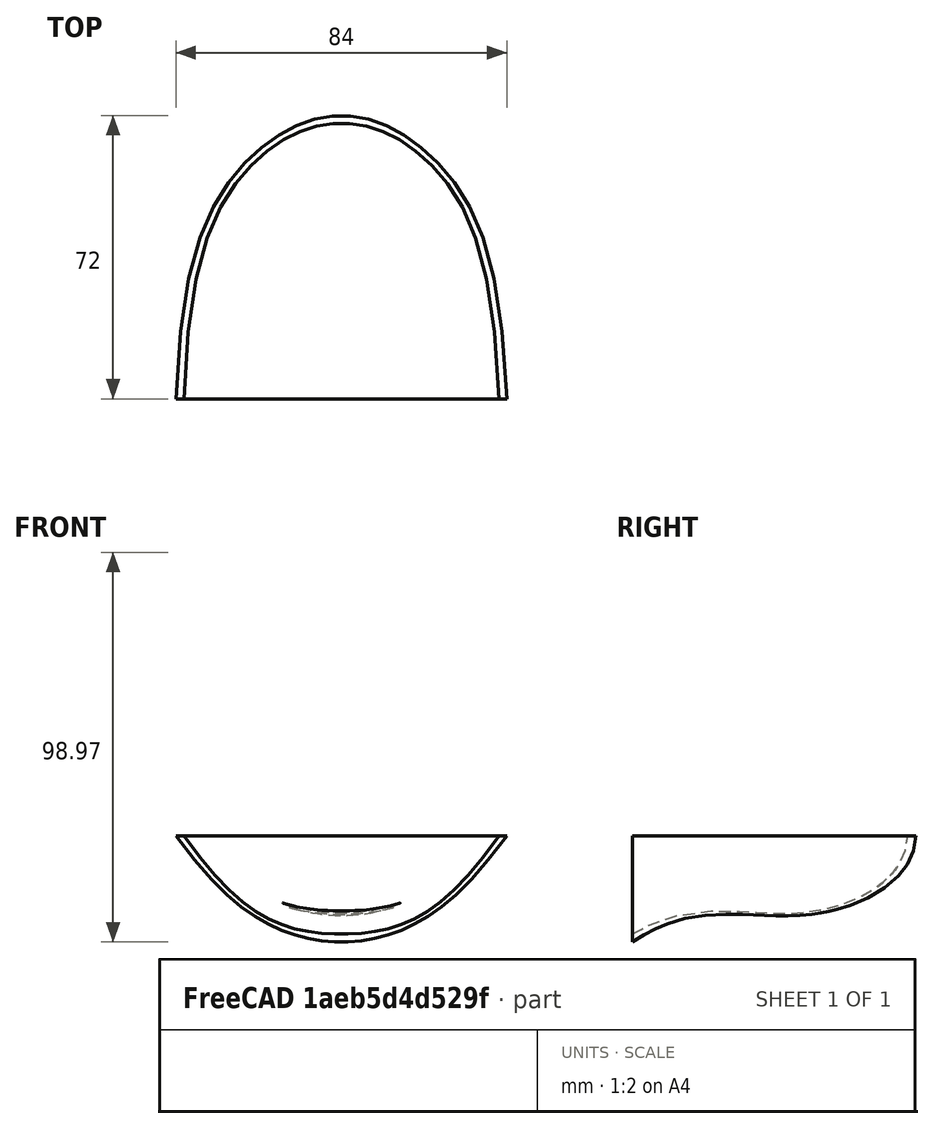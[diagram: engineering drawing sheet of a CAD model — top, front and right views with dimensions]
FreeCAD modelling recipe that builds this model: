
FCSTD DOCUMENT  (FreeCAD 0.21R33771 (Git))
Label: curved_surface_test
License: All rights reserved
LicenseURL: http://en.wikipedia.org/wiki/All_rights_reserved
objects: Sketcher::SketchObject×7, Surface::Filling×2, Part::RuledSurface×2, Part::Compound×1, Part::Feature×1, PartDesign::Body×1
note: 14 computed .brp shape members not serialized (recipe doc carries the construction recipe); baked Part::Feature solids carry a one-line shape summary decoded from their .brp

FEATURE [Sketcher::SketchObject] Sketch
  FullyConstrained = false
  MapMode = 5
  Support = -> [XY_Plane]
  sketch-geometry (13):
    g0-g6: Circle x7 (B-spline internal-alignment scaffolding for g7; pole/knot coordinates omitted)
    g7: BSplineCurve PolesCount=7 KnotsCount=5 Degree=3 IsPeriodic=0
    g8-g12: GeomPoint x5 (B-spline internal-alignment scaffolding for g7; pole/knot coordinates omitted)
  constraints (16):
    c: Weight(g0) = 1
    c: Equal(g0,g1)
    c: Equal(g0,g2)
    c: Equal(g0,g3)
    c: PointOnObject(g3,g-2)
    c: Equal(g0,g4)
    c: Equal(g0,g5)
    c: Equal(g0,g6)
    c: InternalAlignment(g0-g6 -> g7) x7
    c: InternalAlignment(g8-g12 -> g7) x5
    c: Symmetric(g7,g7,g-2)
    c: Symmetric(g1,g5,g-2)
    c: Symmetric(g9,g11,g-2)
    c: DistanceX(g0,g7) = 80
    c: DistanceY(g7,g-1) = 30
    c: DistanceY(g-1,g10) = 40
FEATURE [Sketcher::SketchObject] Sketch001
  FullyConstrained = false
  MapMode = 5
  Placement = pos=(0,0,0) rot=(0.57735,0.57735,0.57735;2.0944rad)
  Support = -> [YZ_Plane]
  sketch-geometry (9):
    g0-g4: Circle x5 (B-spline internal-alignment scaffolding for g5; pole/knot coordinates omitted)
    g5: BSplineCurve PolesCount=5 KnotsCount=3 Degree=3 IsPeriodic=0
    g6: GeomPoint X=40 Y=0 Z=0
    g7: GeomPoint X=11.8063 Y=-19.6266 Z=0
    g8: GeomPoint X=-30 Y=-25 Z=0
  constraints (10):
    c: Weight(g0) = 1
    c: PointOnObject(g5,g-1)
    c: Equal(g0, g1-g4) x4
    c: InternalAlignment(g0-g4 -> g5) x5
    c: InternalAlignment(g6,g5)
    c: InternalAlignment(g7,g5)
    c: InternalAlignment(g8,g5)
    c: DistanceX(g5,g-1) = 30
    c: DistanceX(g-1,g5) = 40
    c: DistanceY(g4,g-1) = 25
FEATURE [Sketcher::SketchObject] Sketch002
  AttachmentOffset = pos=(0,0,30) rot=(0,0,1;0rad)
  FullyConstrained = false
  MapMode = 5
  Placement = pos=(0,-30,-6.7e-15) rot=(1,0,0;1.5708rad)
  Support = -> [XZ_Plane]
  sketch-geometry (13):
    g0-g6: Circle x7 (B-spline internal-alignment scaffolding for g7; pole/knot coordinates omitted)
    g7: BSplineCurve PolesCount=7 KnotsCount=5 Degree=3 IsPeriodic=0
    g8-g12: GeomPoint x5 (B-spline internal-alignment scaffolding for g7; pole/knot coordinates omitted)
  constraints (11):
    c: Weight(g0) = 1
    c: PointOnObject(g7,g-1)
    c: Equal(g0, g1-g6) x6
    c: InternalAlignment(g0-g6 -> g7) x7
    c: InternalAlignment(g8-g12 -> g7) x5
    c: Symmetric(g7,g7,g-2)
    c: PointOnObject(g10,g-2)
    c: Symmetric(g4,g2,g-2)
    c: Symmetric(g5,g1,g-2)
    c: DistanceY(g10,g-1) = 25
    c: DistanceX(g7,g7) = 80
FEATURE [Surface::Filling] Surface
  Anisotropy = false
  BoundaryEdges = -> [Sketch002,Sketch]
  BoundaryOrder = [0,0]
  Degree = 3
  Iterations = 2
  MaximumDegree = 8
  MaximumSegments = 9
  PointsOnCurve = 15
  TolAngular = 0.01
  TolCurvature = 0.1
  Tolerance2d = 1e-05
  Tolerance3d = 0.0001
  UnboundEdges = -> [Sketch001]
  UnboundOrder = [0]
FEATURE [Sketcher::SketchObject] Sketch003
  FullyConstrained = false
  MapMode = 5
  sketch-geometry (13):
    g0-g6: Circle x7 (B-spline internal-alignment scaffolding for g7; pole/knot coordinates omitted)
    g7: BSplineCurve PolesCount=7 KnotsCount=5 Degree=3 IsPeriodic=0
    g8-g12: GeomPoint x5 (B-spline internal-alignment scaffolding for g7; pole/knot coordinates omitted)
  constraints (16):
    c: Weight(g0) = 1
    c: Equal(g0,g1)
    c: Equal(g0,g2)
    c: Equal(g0,g3)
    c: PointOnObject(g3,g-2)
    c: Equal(g0,g4)
    c: Equal(g0,g5)
    c: Equal(g0,g6)
    c: InternalAlignment(g0-g6 -> g7) x7
    c: InternalAlignment(g8-g12 -> g7) x5
    c: Symmetric(g7,g7,g-2)
    c: Symmetric(g1,g5,g-2)
    c: Symmetric(g9,g11,g-2)
    c: DistanceX(g0,g7) = 84
    c: DistanceY(g7,g-1) = 30
    c: DistanceY(g-1,g10) = 42
FEATURE [Sketcher::SketchObject] Sketch004
  FullyConstrained = false
  MapMode = 5
  Placement = pos=(0,0,0) rot=(0.57735,0.57735,0.57735;2.0944rad)
  sketch-geometry (9):
    g0-g4: Circle x5 (B-spline internal-alignment scaffolding for g5; pole/knot coordinates omitted)
    g5: BSplineCurve PolesCount=5 KnotsCount=3 Degree=3 IsPeriodic=0
    g6: GeomPoint X=42 Y=0 Z=0
    g7: GeomPoint X=13.0096 Y=-20.2504 Z=0
    g8: GeomPoint X=-30 Y=-27 Z=0
  constraints (10):
    c: Weight(g0) = 1
    c: PointOnObject(g5,g-1)
    c: Equal(g0, g1-g4) x4
    c: InternalAlignment(g0-g4 -> g5) x5
    c: InternalAlignment(g6,g5)
    c: InternalAlignment(g7,g5)
    c: InternalAlignment(g8,g5)
    c: DistanceX(g5,g-1) = 30
    c: DistanceX(g-1,g5) = 42
    c: DistanceY(g4,g-1) = 27
FEATURE [Sketcher::SketchObject] Sketch005
  AttachmentOffset = pos=(0,0,30) rot=(0,0,1;0rad)
  FullyConstrained = false
  MapMode = 5
  Placement = pos=(0,-30,-7e-15) rot=(1,0,0;1.5708rad)
  sketch-geometry (13):
    g0-g6: Circle x7 (B-spline internal-alignment scaffolding for g7; pole/knot coordinates omitted)
    g7: BSplineCurve PolesCount=7 KnotsCount=5 Degree=3 IsPeriodic=0
    g8-g12: GeomPoint x5 (B-spline internal-alignment scaffolding for g7; pole/knot coordinates omitted)
  constraints (11):
    c: Weight(g0) = 1
    c: PointOnObject(g7,g-1)
    c: Equal(g0, g1-g6) x6
    c: InternalAlignment(g0-g6 -> g7) x7
    c: InternalAlignment(g8-g12 -> g7) x5
    c: Symmetric(g7,g7,g-2)
    c: PointOnObject(g10,g-2)
    c: Symmetric(g4,g2,g-2)
    c: Symmetric(g5,g1,g-2)
    c: DistanceY(g10,g-1) = 27
    c: DistanceX(g7,g7) = 84
FEATURE [Surface::Filling] Surface001
  Anisotropy = false
  BoundaryEdges = -> [Sketch005,Sketch003]
  BoundaryOrder = [0,0]
  Degree = 3
  Iterations = 2
  MaximumDegree = 8
  MaximumSegments = 9
  PointsOnCurve = 15
  TolAngular = 0.01
  TolCurvature = 0.1
  Tolerance2d = 1e-05
  Tolerance3d = 0.0001
  UnboundEdges = -> [Sketch004]
  UnboundOrder = [0]
FEATURE [Part::RuledSurface] Ruled_Surface
  Curve1 = -> Surface [Edge1]
  Curve2 = -> Surface001 [Edge1]
  Orientation = 0
FEATURE [Part::RuledSurface] Ruled_Surface001
  Curve1 = -> Surface001 [Edge2]
  Curve2 = -> Surface [Edge2]
  Orientation = 0
FEATURE [Part::Compound] Compound
  Links = -> [Surface,Surface001,Ruled_Surface001,Ruled_Surface]
FEATURE [Part::Feature] Compound_solid  label="Compound (Solid)"
  shape: bbox 92.7 x 114.7 x 370.3 mm, 4 faces (baked)
FEATURE [Sketcher::SketchObject] Sketch006
  FullyConstrained = false
  MapMode = 5
  Placement = pos=(0,0,0) rot=(0.57735,0.57735,0.57735;2.0944rad)
  Support = -> [YZ_Plane]
  sketch-geometry (3):
    g0: LineSegment StartX=-30 StartY=-26.8366 StartZ=0 EndX=0 EndY=13.6006 EndZ=0
    g1: LineSegment StartX=0 StartY=13.6006 StartZ=0 EndX=-30 EndY=13.6006 EndZ=0
    g2: LineSegment StartX=-30 StartY=13.6006 StartZ=0 EndX=-30 EndY=-26.8366 EndZ=0
  constraints (7):
    c: Coincident(g0,g1)
    c: Horizontal(g1)
    c: Coincident(g1,g2)
    c: Coincident(g2,g0)
    c: Vertical(g2)
    c: PointOnObject(g0,g-2)
    c: DistanceX(g0,g-1) = 30
FEATURE [PartDesign::Body] Body
  Group = -> [Sketch,Sketch001,Sketch002,Sketch006]
  Origin = -> Origin
